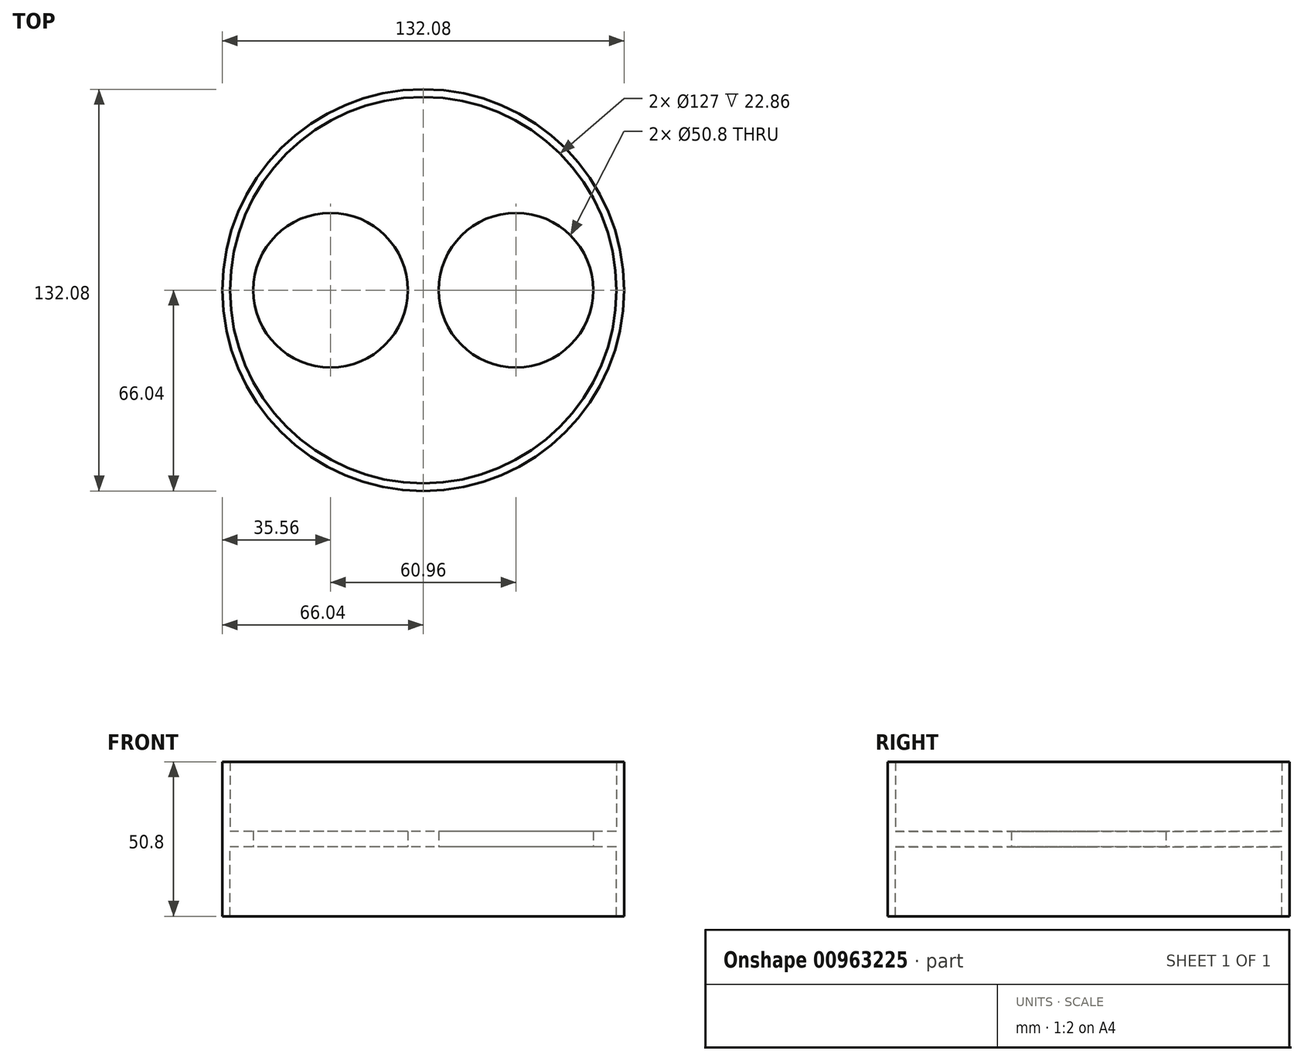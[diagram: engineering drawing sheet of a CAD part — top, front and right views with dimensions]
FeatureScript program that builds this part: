
annotation { "Feature Type Name" : "Feature", "Feature Type Description" : "" }
export const myFeature = defineFeature(function(context is Context, id is Id, definition is map)
    precondition{}
    {
        {
            var Q0;
            Q0=qCreatedBy(makeId("Top.planeOp"),FACE);
            var sketch = newSketch(context, id + "F0", { "sketchPlane" : qUnion([Q0])});
            skCircle(sketch, "E0", {"center": v(0, 0) * mm, "radius": 66.04 * mm});
            skSolve(sketch);
        }
        {
            var Q0;
            Q0 = qSketchRegion(id + "F0", true);
            extrude(context, id + "F1", {"entities" : qUnion([Q0]), "depth" : 25.4 * mm, "offsetDistance" : 25.4 * mm});
        }
        {
            var Q0;
            Q0=makeQuery(id+"F1.opExtrude","CAP_FACE",FACE,{"disambiguationData":[OSD([sQuery(id+"F0.wireOp",EDGE,"E0")])],"isStart":false});
            var sketch = newSketch(context, id + "F2", { "sketchPlane" : qUnion([Q0])});
            skCircle(sketch, "E1", {"center": v(0, 0) * mm, "radius": 63.5 * mm});
            skSolve(sketch);
        }
        {
            var Q0;
            Q0=makeQuery(id+"F1.opExtrude","CAP_FACE",FACE,{"disambiguationData":[OSD([sQuery(id+"F0.wireOp",EDGE,"E0")])],"isStart":false});
            shell(context, id + "F3", {"entities" : qUnion([Q0]), "thickness" : 2.54 * mm});
        }
        {
            var Q0;
            Q0=makeQuery(id+"F1.opExtrude","CAP_FACE",FACE,{"disambiguationData":[OSD([sQuery(id+"F0.wireOp",EDGE,"E0")])],"isStart":true});
            var sketch = newSketch(context, id + "F4", { "sketchPlane" : qUnion([Q0])});
            skCircle(sketch, "E2", {"center": v(30.48, 0) * mm, "radius": 25.4 * mm});
            skCircle(sketch, "E3.MirrorC", {"center": v(-30.48, 0) * mm, "radius": 25.4 * mm});
            skSolve(sketch);
        }
        {
            var Q0;
            Q0=sQuery(id+"F4.wireOp",VERTEX,"E2.center");
            var Q1;
            Q1=sQuery(id+"F4.wireOp",VERTEX,"E3.MirrorC.center");
            var Q2;
            Q2=makeQuery(id+"F1.opExtrude","SWEPT_BODY",BODY,{"disambiguationData":[OSD([sQuery(id+"F0.wireOp",EDGE,"E0")])]});
            hole(context, id + "F5", {"style" : HoleStyle.SIMPLE, "endStyle" : HoleEndStyle.BLIND, "holeDiameter" : 50.8 * mm, "majorDiameter" : 6.35 * mm, "holeDepth" : 127 * mm, "isTappedThrough" : true, "tappedDepth" : 12.7 * mm, "tapClearance" : 3, "startFromSketch" : true, "locations" : qUnion([Q0, Q1]), "scope" : qUnion([Q2])});
        }
        {
            var Q0;
            Q0=makeQuery(id+"F1.opExtrude","SWEPT_BODY",BODY,{"disambiguationData":[OSD([sQuery(id+"F0.wireOp",EDGE,"E0")])]});
            var Q1;
            Q1=makeQuery(id+"F4.imprint","IMPRINT",FACE,{"disambiguationData":[TD([[makeQuery(id+"F4.imprint","IMPRINT",EDGE,{"derivedFrom":sQuery(id+"F4.wireOp",EDGE,"E2")}),-1.0]])]});
            mirror(context, id + "F6", {"operationType" : NewBodyOperationType.ADD, "entities" : qUnion([Q0]), "mirrorPlane" : qUnion([Q1])});
        }
    });
